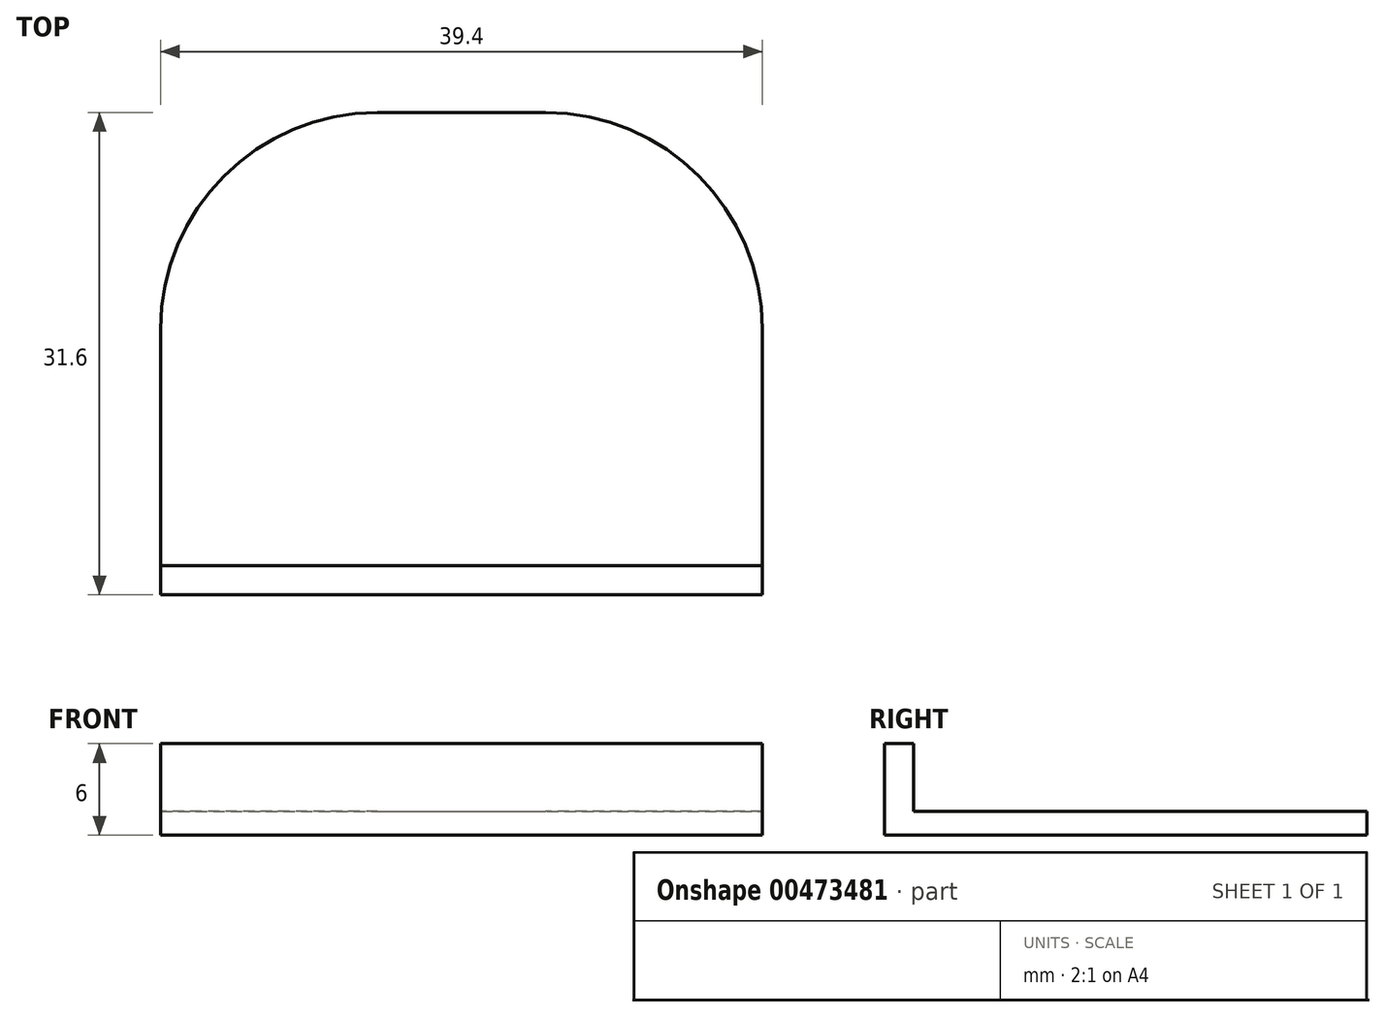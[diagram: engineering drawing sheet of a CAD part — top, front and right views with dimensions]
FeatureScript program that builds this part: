
annotation { "Feature Type Name" : "Feature", "Feature Type Description" : "" }
export const myFeature = defineFeature(function(context is Context, id is Id, definition is map)
    precondition{}
    {
        {
            var Q0;
            Q0=qCreatedBy(makeId("Top.planeOp"),FACE);
            var sketch = newSketch(context, id + "F0", { "sketchPlane" : qUnion([Q0])});
            skLineSegment(sketch, "E0.bottom", {"start": v(0, 0) * mm, "end": v(39.4, 0) * mm});
            skLineSegment(sketch, "E0.top", {"start": v(14.2, 31.6) * mm, "end": v(25.2, 31.6) * mm});
            skLineSegment(sketch, "E0.left", {"start": v(0, 0) * mm, "end": v(0, 17.4) * mm});
            skLineSegment(sketch, "E0.right", {"start": v(39.4, 0) * mm, "end": v(39.4, 17.4) * mm});
            skPoint(sketch, "E1.visualSharp", {"position": v(0, 31.6) * mm});
            skArc(sketch, "E1.filletArc", {"start": v(14.2, 31.6) * mm, "mid": v(4.16, 27.44) * mm, "end": v(0, 17.4) * mm});
            skLineSegment(sketch, "E2", {"start": v(19.7, 0) * mm, "end": v(19.7, 31.6) * mm, "construction": true});
            skArc(sketch, "E3.MirrorCS", {"start": v(25.2, 31.6) * mm, "mid": v(35.24, 27.44) * mm, "end": v(39.4, 17.4) * mm});
            skLineSegment(sketch, "E4", {"start": v(0, 1.9) * mm, "end": v(39.4, 1.9) * mm});
            skSolve(sketch);
        }
        {
            var Q0;
            Q0=makeQuery(id+"F0.imprint","IMPRINT",FACE,{"disambiguationData":[TD([[makeQuery(id+"F0.imprint","IMPRINT",EDGE,{"derivedFrom":sQuery(id+"F0.wireOp",EDGE,"E0.top")}),-1.0]])]});
            extrude(context, id + "F1", {"entities" : qUnion([Q0]), "depth" : 1.55 * mm});
        }
        {
            var Q0;
            {var subQ0=sQuery(id+"F0.wireOp",EDGE,"E0.bottom");Q0=makeQuery(id+"F0.imprint","IMPRINT",FACE,{"disambiguationData":[TD([[makeQuery(id+"F0.imprint","IMPRINT",EDGE,{"derivedFrom":subQ0}),1.0]])]});}
            extrude(context, id + "F2", {"entities" : qUnion([Q0]), "operationType" : NewBodyOperationType.ADD, "depth" : 6 * mm});
        }
    });
